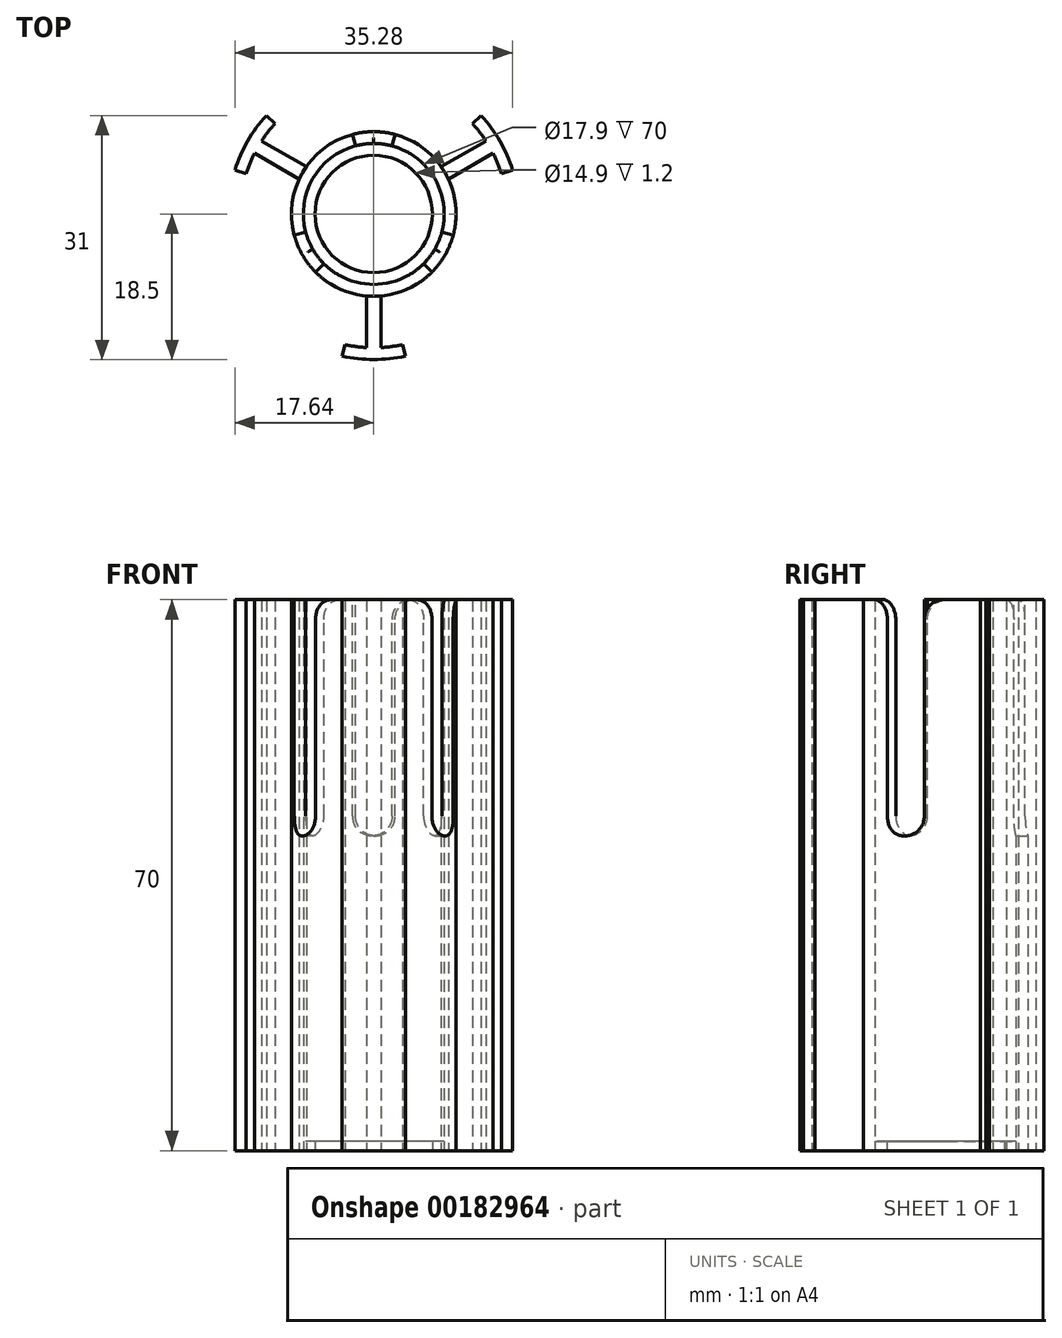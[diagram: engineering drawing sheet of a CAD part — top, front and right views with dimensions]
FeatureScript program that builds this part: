
annotation { "Feature Type Name" : "Feature", "Feature Type Description" : "" }
export const myFeature = defineFeature(function(context is Context, id is Id, definition is map)
    precondition{}
    {
        {
            var Q0;
            Q0=qCreatedBy(makeId("Top.planeOp"),FACE);
            var sketch = newSketch(context, id + "F0", { "sketchPlane" : qUnion([Q0])});
            skCircle(sketch, "E0", {"center": v(0, 0) * mm, "radius": 17 * mm});
            skLineSegment(sketch, "E1", {"start": v(0, 0) * mm, "end": v(0, -72) * mm, "construction": true});
            skCircle(sketch, "E2", {"center": v(0, 0) * mm, "radius": 10.45 * mm});
            skLineSegment(sketch, "E3", {"start": v(52.54, 30.34) * mm, "end": v(0, 0) * mm, "construction": true});
            skLineSegment(sketch, "E4.0", {"start": v(-0.9, -10.41) * mm, "end": v(-0.9, -16.98) * mm});
            skLineSegment(sketch, "E5.0", {"start": v(0.9, -10.41) * mm, "end": v(0.9, -16.98) * mm});
            skCircle(sketch, "E6", {"center": v(0, 0) * mm, "radius": 8.95 * mm});
            skCircle(sketch, "E7", {"center": v(0, 0) * mm, "radius": 18.5 * mm});
            skCircle(sketch, "E8", {"center": v(0, 0) * mm, "radius": 7.45 * mm});
            skLineSegment(sketch, "E9", {"start": v(0, 0) * mm, "end": v(-51.54, 29.76) * mm, "construction": true});
            skLineSegment(sketch, "E10.MirrorCS", {"start": v(8.57, 5.99) * mm, "end": v(14.25, 9.27) * mm});
            skLineSegment(sketch, "E11.MirrorCS", {"start": v(9.47, 4.43) * mm, "end": v(15.15, 7.7) * mm});
            skLineSegment(sketch, "E12.MirrorCS", {"start": v(-9.47, 4.43) * mm, "end": v(-15.15, 7.7) * mm});
            skLineSegment(sketch, "E13.MirrorCS", {"start": v(-8.57, 5.99) * mm, "end": v(-14.25, 9.27) * mm});
            skLineSegment(sketch, "E14", {"start": v(4, -18.06) * mm, "end": v(3.68, -16.6) * mm});
            skLineSegment(sketch, "E15", {"start": v(-4, -18.06) * mm, "end": v(-3.68, -16.6) * mm});
            skLineSegment(sketch, "E16.MirrorCS", {"start": v(13.64, 12.5) * mm, "end": v(12.53, 11.49) * mm});
            skLineSegment(sketch, "E17.MirrorCS", {"start": v(17.64, 5.56) * mm, "end": v(16.21, 5.11) * mm});
            skLineSegment(sketch, "E18.MirrorCS", {"start": v(-17.64, 5.56) * mm, "end": v(-16.21, 5.11) * mm});
            skLineSegment(sketch, "E19.MirrorCS", {"start": v(-13.64, 12.5) * mm, "end": v(-12.53, 11.49) * mm});
            skSolve(sketch);
        }
        {
            var Q0;
            {var subQ0=sQuery(id+"F0.wireOp",EDGE,"E4.0");Q0=makeQuery(id+"F0.imprint","IMPRINT",FACE,{"disambiguationData":[TD([[makeQuery(id+"F0.imprint","IMPRINT",EDGE,{"derivedFrom":subQ0}),1.0]])]});}
            var Q1;
            {var subQ0=sQuery(id+"F0.wireOp",EDGE,"E12.MirrorCS");Q1=makeQuery(id+"F0.imprint","IMPRINT",FACE,{"disambiguationData":[TD([[makeQuery(id+"F0.imprint","IMPRINT",EDGE,{"derivedFrom":subQ0}),-1.0]])]});}
            var Q2;
            {var subQ0=sQuery(id+"F0.wireOp",EDGE,"E14");Q2=makeQuery(id+"F0.imprint","IMPRINT",FACE,{"disambiguationData":[TD([[makeQuery(id+"F0.imprint","IMPRINT",EDGE,{"derivedFrom":subQ0}),1.0]])]});}
            var Q3;
            {var subQ0=sQuery(id+"F0.wireOp",EDGE,"E18.MirrorCS");Q3=makeQuery(id+"F0.imprint","IMPRINT",FACE,{"disambiguationData":[TD([[makeQuery(id+"F0.imprint","IMPRINT",EDGE,{"derivedFrom":subQ0}),1.0]])]});}
            var Q4;
            {var subQ0=sQuery(id+"F0.wireOp",EDGE,"E10.MirrorCS");Q4=makeQuery(id+"F0.imprint","IMPRINT",FACE,{"disambiguationData":[TD([[makeQuery(id+"F0.imprint","IMPRINT",EDGE,{"derivedFrom":subQ0}),-1.0]])]});}
            var Q5;
            {var subQ0=sQuery(id+"F0.wireOp",EDGE,"E16.MirrorCS");Q5=makeQuery(id+"F0.imprint","IMPRINT",FACE,{"disambiguationData":[TD([[makeQuery(id+"F0.imprint","IMPRINT",EDGE,{"derivedFrom":subQ0}),1.0]])]});}
            extrude(context, id + "F1", {"entities" : qUnion([Q0, Q1, Q2, Q3, Q4, Q5]), "depth" : 70 * mm});
        }
        {
            var Q0;
            Q0=makeQuery(id+"F0.imprint","IMPRINT",FACE,{"disambiguationData":[TD([[makeQuery(id+"F0.imprint","IMPRINT",EDGE,{"derivedFrom":sQuery(id+"F0.wireOp",EDGE,"E6")}),1.0]])]});
            extrude(context, id + "F2", {"entities" : qUnion([Q0]), "operationType" : NewBodyOperationType.ADD, "depth" : 1.2 * mm});
        }
        {
            var Q0;
            Q0=makeQuery(id+"F0.imprint","IMPRINT",FACE,{"disambiguationData":[TD([[makeQuery(id+"F0.imprint","IMPRINT",EDGE,{"derivedFrom":sQuery(id+"F0.wireOp",EDGE,"E6")}),-1.0]])]});
            extrude(context, id + "F3", {"entities" : qUnion([Q0]), "depth" : 70 * mm});
        }
        {
            var Q0;
            Q0=makeQuery(id+"F3.opExtrude","CAP_FACE",FACE,{"disambiguationData":[OSD([sQuery(id+"F0.wireOp",EDGE,"E2"),sQuery(id+"F0.wireOp",EDGE,"E6")])],"isStart":false});
            var sketch = newSketch(context, id + "F4", { "sketchPlane" : qUnion([Q0])});
            skCircle(sketch, "E20.0", {"center": v(0, 0) * mm, "radius": 8.95 * mm});
            skCircle(sketch, "E21.0", {"center": v(0, 0) * mm, "radius": 10.45 * mm});
            skLineSegment(sketch, "E22.0", {"start": v(52.54, 30.34) * mm, "end": v(0, 0) * mm, "construction": true});
            skLineSegment(sketch, "E23.0", {"start": v(0, 0) * mm, "end": v(0, -72) * mm, "construction": true});
            skLineSegment(sketch, "E24.0", {"start": v(0, 0) * mm, "end": v(-51.54, 29.76) * mm, "construction": true});
            skLineSegment(sketch, "E25", {"start": v(0, 0) * mm, "end": v(23.02, -13.3) * mm, "construction": true});
            skLineSegment(sketch, "E26", {"start": v(0, 0) * mm, "end": v(-21.36, -12.33) * mm, "construction": true});
            skLineSegment(sketch, "E27", {"start": v(0, 0) * mm, "end": v(0, 25.71) * mm, "construction": true});
            skLineSegment(sketch, "E28", {"start": v(0, 0) * mm, "end": v(-7.39, -7.39) * mm});
            skLineSegment(sketch, "E29", {"start": v(0, 0) * mm, "end": v(-10.1, -2.7) * mm});
            skPoint(sketch, "E30", {"position": v(-6.33, -6.33) * mm});
            skPoint(sketch, "E31", {"position": v(-8.65, -2.32) * mm});
            skLineSegment(sketch, "E32.MirrorCS", {"start": v(0, 0) * mm, "end": v(-10.1, 2.7) * mm});
            skLineSegment(sketch, "E33.MirrorCS", {"start": v(0, 0) * mm, "end": v(7.39, -7.39) * mm});
            skLineSegment(sketch, "E34.MirrorCS", {"start": v(0, 0) * mm, "end": v(10.1, -2.7) * mm});
            skLineSegment(sketch, "E35.MirrorCS", {"start": v(0, 0) * mm, "end": v(-2.7, 10.1) * mm});
            skLineSegment(sketch, "E36.MirrorCS", {"start": v(0, 0) * mm, "end": v(2.7, 10.1) * mm});
            skSolve(sketch);
        }
        {
            var Q0;
            {var subQ0=sQuery(id+"F4.wireOp",EDGE,"E29");var subQ1=sQuery(id+"F4.wireOp",EDGE,"E20.0");var subQ2=makeQuery(id+"F4.imprint","INTERSECT",VERTEX,{"derivedFrom":[subQ1,subQ0]});Q0=makeQuery(id+"F4.imprint","IMPRINT",FACE,{"disambiguationData":[TD([[makeQuery(id+"F4.imprint","IMPRINT",EDGE,{"disambiguationData":[TD([[subQ2,-1.0]])],"derivedFrom":subQ1}),-1.0]])]});}
            var Q1;
            {var subQ0=sQuery(id+"F4.wireOp",EDGE,"E33.MirrorCS");var subQ1=sQuery(id+"F4.wireOp",EDGE,"E20.0");var subQ2=makeQuery(id+"F4.imprint","INTERSECT",VERTEX,{"derivedFrom":[subQ1,subQ0]});Q1=makeQuery(id+"F4.imprint","IMPRINT",FACE,{"disambiguationData":[TD([[makeQuery(id+"F4.imprint","IMPRINT",EDGE,{"disambiguationData":[TD([[subQ2,-1.0]])],"derivedFrom":subQ1}),-1.0]])]});}
            var Q2;
            {var subQ0=sQuery(id+"F4.wireOp",EDGE,"E35.MirrorCS");var subQ1=sQuery(id+"F4.wireOp",EDGE,"E20.0");var subQ2=makeQuery(id+"F4.imprint","INTERSECT",VERTEX,{"derivedFrom":[subQ1,subQ0]});Q2=makeQuery(id+"F4.imprint","IMPRINT",FACE,{"disambiguationData":[TD([[makeQuery(id+"F4.imprint","IMPRINT",EDGE,{"disambiguationData":[TD([[subQ2,1.0]])],"derivedFrom":subQ1}),-1.0]])]});}
            extrude(context, id + "F5", {"entities" : qUnion([Q0, Q1, Q2]), "operationType" : NewBodyOperationType.REMOVE, "oppositeDirection" : true, "depth" : 30 * mm});
        }
        {
            var Q0;
            Q0=makeQuery(id+"F5.boolean.opBoolean","COPY",EDGE,{"derivedFrom":makeQuery(id+"F5.opExtrude","CAP_EDGE",EDGE,{"disambiguationData":[OSD([sQuery(id+"F4.wireOp",EDGE,"E33.MirrorCS")])],"isStart":false})});
            var Q1;
            Q1=makeQuery(id+"F5.boolean.opBoolean","COPY",EDGE,{"derivedFrom":makeQuery(id+"F5.opExtrude","CAP_EDGE",EDGE,{"disambiguationData":[OSD([sQuery(id+"F4.wireOp",EDGE,"E34.MirrorCS")])],"isStart":false})});
            var Q2;
            Q2=makeQuery(id+"F5.boolean.opBoolean","COPY",EDGE,{"derivedFrom":makeQuery(id+"F5.opExtrude","CAP_EDGE",EDGE,{"disambiguationData":[OSD([sQuery(id+"F4.wireOp",EDGE,"E33.MirrorCS")])],"isStart":true})});
            var Q3;
            Q3=makeQuery(id+"F5.boolean.opBoolean","COPY",EDGE,{"derivedFrom":makeQuery(id+"F5.opExtrude","CAP_EDGE",EDGE,{"disambiguationData":[OSD([sQuery(id+"F4.wireOp",EDGE,"E34.MirrorCS")])],"isStart":true})});
            var Q4;
            Q4=makeQuery(id+"F5.boolean.opBoolean","COPY",EDGE,{"derivedFrom":makeQuery(id+"F5.opExtrude","CAP_EDGE",EDGE,{"disambiguationData":[OSD([sQuery(id+"F4.wireOp",EDGE,"E35.MirrorCS")])],"isStart":false})});
            var Q5;
            Q5=makeQuery(id+"F5.boolean.opBoolean","COPY",EDGE,{"derivedFrom":makeQuery(id+"F5.opExtrude","CAP_EDGE",EDGE,{"disambiguationData":[OSD([sQuery(id+"F4.wireOp",EDGE,"E36.MirrorCS")])],"isStart":false})});
            var Q6;
            Q6=makeQuery(id+"F5.boolean.opBoolean","COPY",EDGE,{"derivedFrom":makeQuery(id+"F5.opExtrude","CAP_EDGE",EDGE,{"disambiguationData":[OSD([sQuery(id+"F4.wireOp",EDGE,"E36.MirrorCS")])],"isStart":true})});
            var Q7;
            Q7=makeQuery(id+"F5.boolean.opBoolean","COPY",EDGE,{"derivedFrom":makeQuery(id+"F5.opExtrude","CAP_EDGE",EDGE,{"disambiguationData":[OSD([sQuery(id+"F4.wireOp",EDGE,"E35.MirrorCS")])],"isStart":true})});
            var Q8;
            Q8=makeQuery(id+"F5.boolean.opBoolean","COPY",EDGE,{"derivedFrom":makeQuery(id+"F5.opExtrude","CAP_EDGE",EDGE,{"disambiguationData":[OSD([sQuery(id+"F4.wireOp",EDGE,"E28")])],"isStart":true})});
            var Q9;
            Q9=makeQuery(id+"F5.boolean.opBoolean","COPY",EDGE,{"derivedFrom":makeQuery(id+"F5.opExtrude","CAP_EDGE",EDGE,{"disambiguationData":[OSD([sQuery(id+"F4.wireOp",EDGE,"E29")])],"isStart":true})});
            var Q10;
            Q10=makeQuery(id+"F5.boolean.opBoolean","COPY",EDGE,{"derivedFrom":makeQuery(id+"F5.opExtrude","CAP_EDGE",EDGE,{"disambiguationData":[OSD([sQuery(id+"F4.wireOp",EDGE,"E28")])],"isStart":false})});
            var Q11;
            Q11=makeQuery(id+"F5.boolean.opBoolean","COPY",EDGE,{"derivedFrom":makeQuery(id+"F5.opExtrude","CAP_EDGE",EDGE,{"disambiguationData":[OSD([sQuery(id+"F4.wireOp",EDGE,"E29")])],"isStart":false})});
            fillet(context, id + "F6", {"entities" : qUnion([Q0, Q1, Q2, Q3, Q4, Q5, Q6, Q7, Q8, Q9, Q10, Q11]), "radius" : 2.5 * mm, "tangentPropagation" : true, "allowEdgeOverflow" : false});
        }
    });
